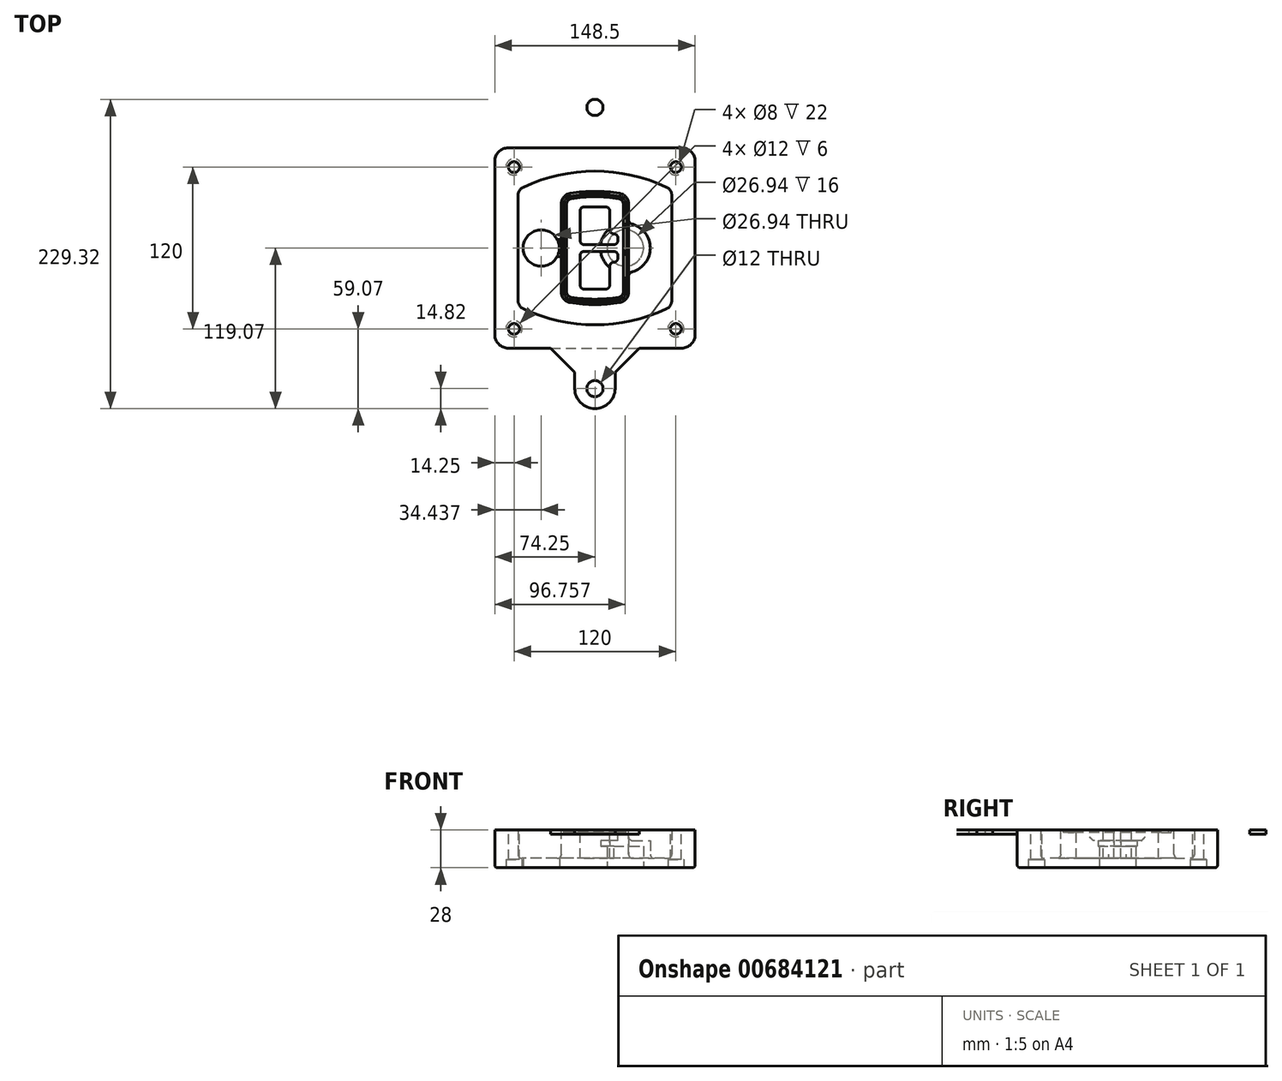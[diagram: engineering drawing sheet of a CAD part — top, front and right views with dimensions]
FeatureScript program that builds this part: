
annotation { "Feature Type Name" : "Feature", "Feature Type Description" : "" }
export const myFeature = defineFeature(function(context is Context, id is Id, definition is map)
    precondition{}
    {
        {
            var Q0;
            Q0=qCreatedBy(makeId("Top.planeOp"),FACE);
            var sketch = newSketch(context, id + "F0", { "sketchPlane" : qUnion([Q0])});
            skPoint(sketch, "E0.rect.middle", {"position": v(0, 0) * mm});
            skLineSegment(sketch, "E1.bottom", {"start": v(-64.25, -74.25) * mm, "end": v(64.25, -74.25) * mm});
            skLineSegment(sketch, "E1.top", {"start": v(-64.25, 74.25) * mm, "end": v(64.25, 74.25) * mm});
            skLineSegment(sketch, "E1.left", {"start": v(-74.25, -64.25) * mm, "end": v(-74.25, 64.25) * mm});
            skLineSegment(sketch, "E1.right", {"start": v(74.25, -64.25) * mm, "end": v(74.25, 64.25) * mm});
            skLineSegment(sketch, "E2", {"start": v(-74.25, 74.25) * mm, "end": v(74.25, -74.25) * mm, "construction": true});
            skLineSegment(sketch, "E3", {"start": v(74.25, 74.25) * mm, "end": v(-74.25, -74.25) * mm, "construction": true});
            skCircle(sketch, "E4", {"center": v(-60, 60) * mm, "radius": 4 * mm});
            skCircle(sketch, "E5", {"center": v(60, 60) * mm, "radius": 4 * mm});
            skCircle(sketch, "E6", {"center": v(60, -60) * mm, "radius": 4 * mm});
            skCircle(sketch, "E7", {"center": v(-60, -60) * mm, "radius": 4 * mm});
            skLineSegment(sketch, "E8", {"start": v(-60, 60) * mm, "end": v(60, 60) * mm, "construction": true});
            skLineSegment(sketch, "E9", {"start": v(60, 60) * mm, "end": v(60, -60) * mm, "construction": true});
            skLineSegment(sketch, "E10", {"start": v(60, -60) * mm, "end": v(-60, -60) * mm, "construction": true});
            skLineSegment(sketch, "E11", {"start": v(-60, -60) * mm, "end": v(-60, 60) * mm, "construction": true});
            skLineSegment(sketch, "E12", {"start": v(-60, 38.83) * mm, "end": v(-60, -38.83) * mm});
            skLineSegment(sketch, "E13", {"start": v(60, 38.83) * mm, "end": v(60, -38.83) * mm});
            skArc(sketch, "E14", {"start": v(54.26, 47.88) * mm, "mid": v(0, 60) * mm, "end": v(-54.26, 47.88) * mm});
            skArc(sketch, "E15", {"start": v(-54.26, -47.88) * mm, "mid": v(0, -60) * mm, "end": v(54.26, -47.88) * mm});
            skLineSegment(sketch, "E16", {"start": v(-60, 0) * mm, "end": v(60, 0) * mm, "construction": true});
            skPoint(sketch, "E17.visualSharp", {"position": v(-60, -45) * mm});
            skArc(sketch, "E17.filletArc", {"start": v(-60, -38.83) * mm, "mid": v(-58.44, -44.2) * mm, "end": v(-54.26, -47.88) * mm});
            skPoint(sketch, "E18.visualSharp", {"position": v(-60, 45) * mm});
            skArc(sketch, "E18.filletArc", {"start": v(-54.26, 47.88) * mm, "mid": v(-58.44, 44.2) * mm, "end": v(-60, 38.83) * mm});
            skPoint(sketch, "E19.visualSharp", {"position": v(60, 45) * mm});
            skArc(sketch, "E19.filletArc", {"start": v(60, 38.83) * mm, "mid": v(58.44, 44.2) * mm, "end": v(54.26, 47.88) * mm});
            skPoint(sketch, "E20.visualSharp", {"position": v(60, -45) * mm});
            skArc(sketch, "E20.filletArc", {"start": v(54.26, -47.88) * mm, "mid": v(58.44, -44.2) * mm, "end": v(60, -38.83) * mm});
            skPoint(sketch, "E21.visualSharp", {"position": v(-74.25, 74.25) * mm});
            skArc(sketch, "E21.filletArc", {"start": v(-64.25, 74.25) * mm, "mid": v(-71.32, 71.32) * mm, "end": v(-74.25, 64.25) * mm});
            skPoint(sketch, "E22.visualSharp", {"position": v(74.25, 74.25) * mm});
            skArc(sketch, "E22.filletArc", {"start": v(74.25, 64.25) * mm, "mid": v(71.32, 71.32) * mm, "end": v(64.25, 74.25) * mm});
            skPoint(sketch, "E23.visualSharp", {"position": v(74.25, -74.25) * mm});
            skArc(sketch, "E23.filletArc", {"start": v(64.25, -74.25) * mm, "mid": v(71.32, -71.32) * mm, "end": v(74.25, -64.25) * mm});
            skPoint(sketch, "E24.visualSharp", {"position": v(-74.25, -74.25) * mm});
            skArc(sketch, "E24.filletArc", {"start": v(-74.25, -64.25) * mm, "mid": v(-71.32, -71.32) * mm, "end": v(-64.25, -74.25) * mm});
            skArc(sketch, "E25.0", {"start": v(57, 38.83) * mm, "mid": v(55.9, 42.58) * mm, "end": v(52.98, 45.17) * mm});
            skLineSegment(sketch, "E25.1", {"start": v(57, 38.83) * mm, "end": v(57, -38.83) * mm});
            skArc(sketch, "E25.2", {"start": v(52.98, -45.17) * mm, "mid": v(55.9, -42.58) * mm, "end": v(57, -38.83) * mm});
            skArc(sketch, "E25.3", {"start": v(-52.98, -45.17) * mm, "mid": v(0, -57) * mm, "end": v(52.98, -45.17) * mm});
            skArc(sketch, "E25.4", {"start": v(-57, -38.83) * mm, "mid": v(-55.9, -42.58) * mm, "end": v(-52.98, -45.17) * mm});
            skArc(sketch, "E25.5", {"start": v(52.98, 45.17) * mm, "mid": v(0, 57) * mm, "end": v(-52.98, 45.17) * mm});
            skLineSegment(sketch, "E25.6", {"start": v(-57, 38.83) * mm, "end": v(-57, -38.83) * mm});
            skArc(sketch, "E25.7", {"start": v(-52.98, 45.17) * mm, "mid": v(-55.9, 42.58) * mm, "end": v(-57, 38.83) * mm});
            skArc(sketch, "E26.0", {"start": v(-55.96, 51.5) * mm, "mid": v(-61.82, 46.33) * mm, "end": v(-64, 38.83) * mm});
            skArc(sketch, "E26.1", {"start": v(55.96, 51.5) * mm, "mid": v(0, 64) * mm, "end": v(-55.96, 51.5) * mm});
            skArc(sketch, "E26.2", {"start": v(64, 38.83) * mm, "mid": v(61.82, 46.33) * mm, "end": v(55.96, 51.5) * mm});
            skLineSegment(sketch, "E26.3", {"start": v(64, 38.83) * mm, "end": v(64, -38.83) * mm});
            skArc(sketch, "E26.4", {"start": v(55.96, -51.5) * mm, "mid": v(61.82, -46.33) * mm, "end": v(64, -38.83) * mm});
            skLineSegment(sketch, "E26.5", {"start": v(-64, 38.83) * mm, "end": v(-64, -38.83) * mm});
            skArc(sketch, "E26.6", {"start": v(-55.96, -51.5) * mm, "mid": v(0, -64) * mm, "end": v(55.96, -51.5) * mm});
            skArc(sketch, "E26.7", {"start": v(-64, -38.83) * mm, "mid": v(-61.82, -46.33) * mm, "end": v(-55.96, -51.5) * mm});
            skSolve(sketch);
        }
        {
            var Q0;
            Q0=makeQuery(id+"F0.imprint","IMPRINT",FACE,{"disambiguationData":[TD([[makeQuery(id+"F0.imprint","IMPRINT",EDGE,{"derivedFrom":sQuery(id+"F0.wireOp",EDGE,"E1.bottom")}),1.0]])]});
            var Q1;
            Q1=makeQuery(id+"F0.imprint","IMPRINT",FACE,{"disambiguationData":[TD([[makeQuery(id+"F0.imprint","IMPRINT",EDGE,{"derivedFrom":sQuery(id+"F0.wireOp",EDGE,"E12")}),1.0]])]});
            var Q2;
            Q2=makeQuery(id+"F0.imprint","IMPRINT",FACE,{"disambiguationData":[TD([[makeQuery(id+"F0.imprint","IMPRINT",EDGE,{"derivedFrom":sQuery(id+"F0.wireOp",EDGE,"E25.0")}),1.0]])]});
            var Q3;
            Q3=makeQuery(id+"F0.imprint","IMPRINT",FACE,{"disambiguationData":[TD([[makeQuery(id+"F0.imprint","IMPRINT",EDGE,{"derivedFrom":sQuery(id+"F0.wireOp",EDGE,"E12")}),-1.0]])]});
            extrude(context, id + "F1", {"entities" : qUnion([Q0, Q1, Q2, Q3]), "oppositeDirection" : true, "depth" : 25 * mm, "offsetDistance" : 25 * mm});
        }
        {
            var Q0;
            Q0=makeQuery(id+"F0.imprint","IMPRINT",FACE,{"disambiguationData":[TD([[makeQuery(id+"F0.imprint","IMPRINT",EDGE,{"derivedFrom":sQuery(id+"F0.wireOp",EDGE,"E12")}),1.0]])]});
            extrude(context, id + "F2", {"entities" : qUnion([Q0]), "operationType" : NewBodyOperationType.ADD, "depth" : 3 * mm});
        }
        {
            var Q0;
            Q0=makeQuery(id+"F0.imprint","IMPRINT",FACE,{"disambiguationData":[TD([[makeQuery(id+"F0.imprint","IMPRINT",EDGE,{"derivedFrom":sQuery(id+"F0.wireOp",EDGE,"E25.0")}),1.0]])]});
            extrude(context, id + "F3", {"entities" : qUnion([Q0]), "operationType" : NewBodyOperationType.REMOVE, "oppositeDirection" : true, "depth" : 18 * mm});
        }
        {
            var Q0;
            Q0=makeQuery(id+"F2.opExtrude","CAP_FACE",FACE,{"disambiguationData":[OSD([sQuery(id+"F0.wireOp",EDGE,"E12"),sQuery(id+"F0.wireOp",EDGE,"E13"),sQuery(id+"F0.wireOp",EDGE,"E14"),sQuery(id+"F0.wireOp",EDGE,"E15"),sQuery(id+"F0.wireOp",EDGE,"E17.filletArc"),sQuery(id+"F0.wireOp",EDGE,"E18.filletArc"),sQuery(id+"F0.wireOp",EDGE,"E19.filletArc"),sQuery(id+"F0.wireOp",EDGE,"E20.filletArc"),sQuery(id+"F0.wireOp",EDGE,"E25.0"),sQuery(id+"F0.wireOp",EDGE,"E25.1"),sQuery(id+"F0.wireOp",EDGE,"E25.2"),sQuery(id+"F0.wireOp",EDGE,"E25.3"),sQuery(id+"F0.wireOp",EDGE,"E25.4"),sQuery(id+"F0.wireOp",EDGE,"E25.5"),sQuery(id+"F0.wireOp",EDGE,"E25.6"),sQuery(id+"F0.wireOp",EDGE,"E25.7")])],"isStart":false});
            var sketch = newSketch(context, id + "F4", { "sketchPlane" : qUnion([Q0])});
            skArc(sketch, "E27.0", {"start": v(-18.34, -40.45) * mm, "mid": v(0, -42) * mm, "end": v(18.34, -40.45) * mm});
            skArc(sketch, "E28.0", {"start": v(18.34, 40.45) * mm, "mid": v(0, 42) * mm, "end": v(-18.34, 40.45) * mm});
            skLineSegment(sketch, "E29", {"start": v(-25, 32.57) * mm, "end": v(-25, -32.57) * mm});
            skLineSegment(sketch, "E30", {"start": v(25, 32.57) * mm, "end": v(25, -32.57) * mm});
            skLineSegment(sketch, "E31", {"start": v(-25, 39.1) * mm, "end": v(25, 39.1) * mm, "construction": true});
            skLineSegment(sketch, "E32", {"start": v(-25, -39.1) * mm, "end": v(25, -39.1) * mm, "construction": true});
            skPoint(sketch, "E33.visualSharp", {"position": v(-25, 39.1) * mm});
            skArc(sketch, "E33.filletArc", {"start": v(-18.34, 40.45) * mm, "mid": v(-23.11, 37.73) * mm, "end": v(-25, 32.57) * mm});
            skPoint(sketch, "E34.visualSharp", {"position": v(25, 39.1) * mm});
            skArc(sketch, "E34.filletArc", {"start": v(25, 32.57) * mm, "mid": v(23.11, 37.73) * mm, "end": v(18.34, 40.45) * mm});
            skPoint(sketch, "E35.visualSharp", {"position": v(25, -39.1) * mm});
            skArc(sketch, "E35.filletArc", {"start": v(18.34, -40.45) * mm, "mid": v(23.11, -37.73) * mm, "end": v(25, -32.57) * mm});
            skPoint(sketch, "E36.visualSharp", {"position": v(-25, -39.1) * mm});
            skArc(sketch, "E36.filletArc", {"start": v(-25, -32.57) * mm, "mid": v(-23.11, -37.73) * mm, "end": v(-18.34, -40.45) * mm});
            skArc(sketch, "E37.0", {"start": v(52.98, 45.17) * mm, "mid": v(0, 57) * mm, "end": v(-52.98, 45.17) * mm});
            skArc(sketch, "E37.1", {"start": v(-52.98, 45.17) * mm, "mid": v(-55.9, 42.58) * mm, "end": v(-57, 38.83) * mm});
            skLineSegment(sketch, "E37.2", {"start": v(-57, 38.83) * mm, "end": v(-57, -38.83) * mm});
            skArc(sketch, "E37.3", {"start": v(-57, -38.83) * mm, "mid": v(-55.9, -42.58) * mm, "end": v(-52.98, -45.17) * mm});
            skArc(sketch, "E37.4", {"start": v(-52.98, -45.17) * mm, "mid": v(0, -57) * mm, "end": v(52.98, -45.17) * mm});
            skArc(sketch, "E37.5", {"start": v(52.98, -45.17) * mm, "mid": v(55.9, -42.58) * mm, "end": v(57, -38.83) * mm});
            skLineSegment(sketch, "E37.6", {"start": v(57, 38.83) * mm, "end": v(57, -38.83) * mm});
            skArc(sketch, "E37.7", {"start": v(57, 38.83) * mm, "mid": v(55.9, 42.58) * mm, "end": v(52.98, 45.17) * mm});
            skLineSegment(sketch, "E38.0", {"start": v(23, 32.57) * mm, "end": v(23, -32.57) * mm});
            skArc(sketch, "E38.1", {"start": v(18, -38.48) * mm, "mid": v(21.58, -36.44) * mm, "end": v(23, -32.57) * mm});
            skArc(sketch, "E38.2", {"start": v(-18, -38.48) * mm, "mid": v(0, -40) * mm, "end": v(18, -38.48) * mm});
            skArc(sketch, "E38.3", {"start": v(-23, -32.57) * mm, "mid": v(-21.58, -36.44) * mm, "end": v(-18, -38.48) * mm});
            skLineSegment(sketch, "E38.4", {"start": v(-23, 32.57) * mm, "end": v(-23, -32.57) * mm});
            skArc(sketch, "E38.5", {"start": v(23, 32.57) * mm, "mid": v(21.58, 36.44) * mm, "end": v(18, 38.48) * mm});
            skArc(sketch, "E38.6", {"start": v(-18, 38.48) * mm, "mid": v(-21.58, 36.44) * mm, "end": v(-23, 32.57) * mm});
            skArc(sketch, "E38.7", {"start": v(18, 38.48) * mm, "mid": v(0, 40) * mm, "end": v(-18, 38.48) * mm});
            skArc(sketch, "E39.0", {"start": v(21, 32.57) * mm, "mid": v(20.06, 35.15) * mm, "end": v(17.67, 36.5) * mm});
            skLineSegment(sketch, "E39.1", {"start": v(21, 32.57) * mm, "end": v(21, -32.57) * mm});
            skArc(sketch, "E39.2", {"start": v(17.67, -36.5) * mm, "mid": v(20.06, -35.15) * mm, "end": v(21, -32.57) * mm});
            skArc(sketch, "E39.3", {"start": v(-17.67, -36.5) * mm, "mid": v(0, -38) * mm, "end": v(17.67, -36.5) * mm});
            skArc(sketch, "E39.4", {"start": v(-21, -32.57) * mm, "mid": v(-20.06, -35.15) * mm, "end": v(-17.67, -36.5) * mm});
            skArc(sketch, "E39.5", {"start": v(17.67, 36.5) * mm, "mid": v(0, 38) * mm, "end": v(-17.67, 36.5) * mm});
            skLineSegment(sketch, "E39.6", {"start": v(-21, 32.57) * mm, "end": v(-21, -32.57) * mm});
            skArc(sketch, "E39.7", {"start": v(-17.67, 36.5) * mm, "mid": v(-20.06, 35.15) * mm, "end": v(-21, 32.57) * mm});
            skLineSegment(sketch, "E40", {"start": v(-25, 0) * mm, "end": v(25, 0) * mm, "construction": true});
            skLineSegment(sketch, "E41", {"start": v(-11, 5.5) * mm, "end": v(-11, 27.5) * mm});
            skLineSegment(sketch, "E42", {"start": v(-8, 30.5) * mm, "end": v(8, 30.5) * mm});
            skLineSegment(sketch, "E43", {"start": v(11, 27.5) * mm, "end": v(11, 13.5) * mm});
            skLineSegment(sketch, "E44", {"start": v(14, 10.5) * mm, "end": v(14, 10.5) * mm});
            skLineSegment(sketch, "E45", {"start": v(17, 7.5) * mm, "end": v(17, 5.5) * mm});
            skLineSegment(sketch, "E46", {"start": v(14, 2.5) * mm, "end": v(-8, 2.5) * mm});
            skPoint(sketch, "E47.visualSharp", {"position": v(-11, 30.5) * mm});
            skArc(sketch, "E47.filletArc", {"start": v(-8, 30.5) * mm, "mid": v(-10.12, 29.62) * mm, "end": v(-11, 27.5) * mm});
            skPoint(sketch, "E48.visualSharp", {"position": v(11, 30.5) * mm});
            skArc(sketch, "E48.filletArc", {"start": v(11, 27.5) * mm, "mid": v(10.12, 29.62) * mm, "end": v(8, 30.5) * mm});
            skPoint(sketch, "E49.visualSharp", {"position": v(11, 10.5) * mm});
            skArc(sketch, "E49.filletArc", {"start": v(11, 13.5) * mm, "mid": v(11.88, 11.38) * mm, "end": v(14, 10.5) * mm});
            skPoint(sketch, "E50.visualSharp", {"position": v(17, 10.5) * mm});
            skArc(sketch, "E50.filletArc", {"start": v(17, 7.5) * mm, "mid": v(16.12, 9.62) * mm, "end": v(14, 10.5) * mm});
            skPoint(sketch, "E51.visualSharp", {"position": v(17, 2.5) * mm});
            skArc(sketch, "E51.filletArc", {"start": v(14, 2.5) * mm, "mid": v(16.12, 3.38) * mm, "end": v(17, 5.5) * mm});
            skPoint(sketch, "E52.visualSharp", {"position": v(-11, 2.5) * mm});
            skArc(sketch, "E52.filletArc", {"start": v(-11, 5.5) * mm, "mid": v(-10.12, 3.38) * mm, "end": v(-8, 2.5) * mm});
            skLineSegment(sketch, "E53.0.MirrorCS", {"start": v(14, -2.5) * mm, "end": v(-8, -2.5) * mm});
            skArc(sketch, "E54.0.MirrorCS", {"start": v(-11, -5.5) * mm, "mid": v(-10.12, -3.38) * mm, "end": v(-8, -2.5) * mm});
            skLineSegment(sketch, "E55.0.MirrorCS", {"start": v(-11, -5.5) * mm, "end": v(-11, -27.5) * mm});
            skArc(sketch, "E56.0.MirrorCS", {"start": v(-8, -30.5) * mm, "mid": v(-10.12, -29.62) * mm, "end": v(-11, -27.5) * mm});
            skLineSegment(sketch, "E57.0.MirrorCS", {"start": v(-8, -30.5) * mm, "end": v(8, -30.5) * mm});
            skArc(sketch, "E58.0.MirrorCS", {"start": v(11, -27.5) * mm, "mid": v(10.12, -29.62) * mm, "end": v(8, -30.5) * mm});
            skLineSegment(sketch, "E59.0.MirrorCS", {"start": v(11, -27.5) * mm, "end": v(11, -13.5) * mm});
            skArc(sketch, "E60.0.MirrorCS", {"start": v(11, -13.5) * mm, "mid": v(11.88, -11.38) * mm, "end": v(14, -10.5) * mm});
            skArc(sketch, "E61.0.MirrorCS", {"start": v(17, -7.5) * mm, "mid": v(16.12, -9.62) * mm, "end": v(14, -10.5) * mm});
            skLineSegment(sketch, "E62.0.MirrorCS", {"start": v(17, -7.5) * mm, "end": v(17, -5.5) * mm});
            skArc(sketch, "E63.0.MirrorCS", {"start": v(14, -2.5) * mm, "mid": v(16.12, -3.38) * mm, "end": v(17, -5.5) * mm});
            skSolve(sketch);
        }
        {
            var Q0;
            Q0=makeQuery(id+"F4.imprint","IMPRINT",FACE,{"disambiguationData":[TD([[makeQuery(id+"F4.imprint","IMPRINT",EDGE,{"derivedFrom":sQuery(id+"F4.wireOp",EDGE,"E27.0")}),1.0]])]});
            var Q1;
            Q1=makeQuery(id+"F4.imprint","IMPRINT",FACE,{"disambiguationData":[TD([[makeQuery(id+"F4.imprint","IMPRINT",EDGE,{"derivedFrom":sQuery(id+"F4.wireOp",EDGE,"E38.0")}),-1.0]])]});
            var Q2;
            Q2=makeQuery(id+"F4.imprint","IMPRINT",FACE,{"disambiguationData":[TD([[makeQuery(id+"F4.imprint","IMPRINT",EDGE,{"derivedFrom":sQuery(id+"F4.wireOp",EDGE,"E39.0")}),1.0]])]});
            extrude(context, id + "F5", {"entities" : qUnion([Q0, Q1, Q2]), "operationType" : NewBodyOperationType.ADD, "endBound" : BoundingType.UP_TO_NEXT, "oppositeDirection" : true, "depth" : 25 * mm});
        }
        {
            var Q0;
            Q0=makeQuery(id+"F4.imprint","IMPRINT",FACE,{"disambiguationData":[TD([[makeQuery(id+"F4.imprint","IMPRINT",EDGE,{"derivedFrom":sQuery(id+"F4.wireOp",EDGE,"E38.0")}),-1.0]])]});
            extrude(context, id + "F6", {"entities" : qUnion([Q0]), "operationType" : NewBodyOperationType.REMOVE, "oppositeDirection" : true, "depth" : 2 * mm});
        }
        {
            var Q0;
            Q0=makeQuery(id+"F1.opExtrude","CAP_FACE",FACE,{"disambiguationData":[OSD([sQuery(id+"F0.wireOp",EDGE,"E1.bottom"),sQuery(id+"F0.wireOp",EDGE,"E1.top"),sQuery(id+"F0.wireOp",EDGE,"E1.left"),sQuery(id+"F0.wireOp",EDGE,"E1.right"),sQuery(id+"F0.wireOp",EDGE,"E4"),sQuery(id+"F0.wireOp",EDGE,"E5"),sQuery(id+"F0.wireOp",EDGE,"E6"),sQuery(id+"F0.wireOp",EDGE,"E7"),sQuery(id+"F0.wireOp",EDGE,"E21.filletArc"),sQuery(id+"F0.wireOp",EDGE,"E22.filletArc"),sQuery(id+"F0.wireOp",EDGE,"E23.filletArc"),sQuery(id+"F0.wireOp",EDGE,"E24.filletArc")])],"isStart":false});
            var sketch = newSketch(context, id + "F7", { "sketchPlane" : qUnion([Q0])});
            skCircle(sketch, "E64", {"center": v(22.5, 0) * mm, "radius": 13.47 * mm});
            skCircle(sketch, "E65", {"center": v(-39.81, 0) * mm, "radius": 13.47 * mm});
            skLineSegment(sketch, "E66", {"start": v(74.25, 0) * mm, "end": v(-74.25, 0) * mm});
            skCircle(sketch, "E67", {"center": v(22.5, 0) * mm, "radius": 18.47 * mm});
            skCircle(sketch, "E68", {"center": v(60, -60) * mm, "radius": 6 * mm});
            skCircle(sketch, "E69", {"center": v(-60, -60) * mm, "radius": 6 * mm});
            skCircle(sketch, "E70", {"center": v(-60, 60) * mm, "radius": 6 * mm});
            skCircle(sketch, "E71", {"center": v(60, 60) * mm, "radius": 6 * mm});
            skSolve(sketch);
        }
        {
            var Q0;
            {var subQ1=sQuery(id+"F7.wireOp",EDGE,"E66");var subQ4=sQuery(id+"F7.wireOp",EDGE,"E64");var subQ6=makeQuery(id+"F7.imprint","INTERSECT",VERTEX,{"disambiguationData":[OD(0.0)],"derivedFrom":[subQ4,subQ1]});Q0=makeQuery(id+"F7.imprint","IMPRINT",FACE,{"disambiguationData":[TD([[makeQuery(id+"F7.imprint","IMPRINT",EDGE,{"disambiguationData":[TD([[subQ6,-1.0]])],"derivedFrom":subQ4}),-1.0]])]});}
            var Q1;
            {var subQ0=sQuery(id+"F7.wireOp",EDGE,"E66");var subQ1=sQuery(id+"F7.wireOp",EDGE,"E64");var subQ3=makeQuery(id+"F7.imprint","INTERSECT",VERTEX,{"disambiguationData":[OD(0.0)],"derivedFrom":[subQ1,subQ0]});Q1=makeQuery(id+"F7.imprint","IMPRINT",FACE,{"disambiguationData":[TD([[makeQuery(id+"F7.imprint","IMPRINT",EDGE,{"disambiguationData":[TD([[subQ3,-1.0]])],"derivedFrom":subQ1}),1.0]])]});}
            var Q2;
            {var subQ0=sQuery(id+"F7.wireOp",EDGE,"E66");var subQ1=sQuery(id+"F7.wireOp",EDGE,"E64");var subQ3=makeQuery(id+"F7.imprint","INTERSECT",VERTEX,{"disambiguationData":[OD(0.0)],"derivedFrom":[subQ1,subQ0]});Q2=makeQuery(id+"F7.imprint","IMPRINT",FACE,{"disambiguationData":[TD([[makeQuery(id+"F7.imprint","IMPRINT",EDGE,{"disambiguationData":[TD([[subQ3,1.0]])],"derivedFrom":subQ1}),1.0]])]});}
            var Q3;
            {var subQ1=sQuery(id+"F7.wireOp",EDGE,"E66");var subQ4=sQuery(id+"F7.wireOp",EDGE,"E64");var subQ6=makeQuery(id+"F7.imprint","INTERSECT",VERTEX,{"disambiguationData":[OD(0.0)],"derivedFrom":[subQ4,subQ1]});Q3=makeQuery(id+"F7.imprint","IMPRINT",FACE,{"disambiguationData":[TD([[makeQuery(id+"F7.imprint","IMPRINT",EDGE,{"disambiguationData":[TD([[subQ6,1.0]])],"derivedFrom":subQ4}),-1.0]])]});}
            extrude(context, id + "F8", {"entities" : qUnion([Q0, Q1, Q2, Q3]), "operationType" : NewBodyOperationType.ADD, "oppositeDirection" : true, "depth" : 20 * mm});
        }
        {
            var Q0;
            {var subQ0=sQuery(id+"F7.wireOp",EDGE,"E66");var subQ1=sQuery(id+"F7.wireOp",EDGE,"E64");var subQ3=makeQuery(id+"F7.imprint","INTERSECT",VERTEX,{"disambiguationData":[OD(0.0)],"derivedFrom":[subQ1,subQ0]});Q0=makeQuery(id+"F7.imprint","IMPRINT",FACE,{"disambiguationData":[TD([[makeQuery(id+"F7.imprint","IMPRINT",EDGE,{"disambiguationData":[TD([[subQ3,-1.0]])],"derivedFrom":subQ1}),1.0]])]});}
            var Q1;
            {var subQ0=sQuery(id+"F7.wireOp",EDGE,"E66");var subQ1=sQuery(id+"F7.wireOp",EDGE,"E64");var subQ3=makeQuery(id+"F7.imprint","INTERSECT",VERTEX,{"disambiguationData":[OD(0.0)],"derivedFrom":[subQ1,subQ0]});Q1=makeQuery(id+"F7.imprint","IMPRINT",FACE,{"disambiguationData":[TD([[makeQuery(id+"F7.imprint","IMPRINT",EDGE,{"disambiguationData":[TD([[subQ3,1.0]])],"derivedFrom":subQ1}),1.0]])]});}
            extrude(context, id + "F9", {"entities" : qUnion([Q0, Q1]), "operationType" : NewBodyOperationType.REMOVE, "oppositeDirection" : true, "depth" : 16 * mm});
        }
        {
            var Q0;
            {var subQ0=sQuery(id+"F7.wireOp",EDGE,"E66");var subQ1=sQuery(id+"F7.wireOp",EDGE,"E65");var subQ3=makeQuery(id+"F7.imprint","INTERSECT",VERTEX,{"disambiguationData":[OD(0.0)],"derivedFrom":[subQ1,subQ0]});Q0=makeQuery(id+"F7.imprint","IMPRINT",FACE,{"disambiguationData":[TD([[makeQuery(id+"F7.imprint","IMPRINT",EDGE,{"disambiguationData":[TD([[subQ3,-1.0]])],"derivedFrom":subQ1}),1.0]])]});}
            var Q1;
            {var subQ0=sQuery(id+"F7.wireOp",EDGE,"E66");var subQ1=sQuery(id+"F7.wireOp",EDGE,"E65");var subQ3=makeQuery(id+"F7.imprint","INTERSECT",VERTEX,{"disambiguationData":[OD(0.0)],"derivedFrom":[subQ1,subQ0]});Q1=makeQuery(id+"F7.imprint","IMPRINT",FACE,{"disambiguationData":[TD([[makeQuery(id+"F7.imprint","IMPRINT",EDGE,{"disambiguationData":[TD([[subQ3,1.0]])],"derivedFrom":subQ1}),1.0]])]});}
            extrude(context, id + "F10", {"entities" : qUnion([Q0, Q1]), "operationType" : NewBodyOperationType.REMOVE, "oppositeDirection" : true, "depth" : 25 * mm});
        }
        {
            var Q0;
            Q0=makeQuery(id+"F7.imprint","IMPRINT",FACE,{"disambiguationData":[TD([[makeQuery(id+"F7.imprint","IMPRINT",EDGE,{"derivedFrom":sQuery(id+"F7.wireOp",EDGE,"E68")}),1.0]])]});
            var Q1;
            Q1=makeQuery(id+"F7.imprint","IMPRINT",FACE,{"disambiguationData":[TD([[makeQuery(id+"F7.imprint","IMPRINT",EDGE,{"derivedFrom":makeQuery(id+"F1.opExtrude","CAP_EDGE",EDGE,{"disambiguationData":[OSD([sQuery(id+"F0.wireOp",EDGE,"E5")])],"isStart":false})}),-1.0]])]});
            var Q2;
            Q2=makeQuery(id+"F7.imprint","IMPRINT",FACE,{"disambiguationData":[TD([[makeQuery(id+"F7.imprint","IMPRINT",EDGE,{"derivedFrom":sQuery(id+"F7.wireOp",EDGE,"E69")}),1.0]])]});
            var Q3;
            Q3=makeQuery(id+"F7.imprint","IMPRINT",FACE,{"disambiguationData":[TD([[makeQuery(id+"F7.imprint","IMPRINT",EDGE,{"derivedFrom":makeQuery(id+"F1.opExtrude","CAP_EDGE",EDGE,{"disambiguationData":[OSD([sQuery(id+"F0.wireOp",EDGE,"E4")])],"isStart":false})}),-1.0]])]});
            var Q4;
            Q4=makeQuery(id+"F7.imprint","IMPRINT",FACE,{"disambiguationData":[TD([[makeQuery(id+"F7.imprint","IMPRINT",EDGE,{"derivedFrom":sQuery(id+"F7.wireOp",EDGE,"E70")}),1.0]])]});
            var Q5;
            Q5=makeQuery(id+"F7.imprint","IMPRINT",FACE,{"disambiguationData":[TD([[makeQuery(id+"F7.imprint","IMPRINT",EDGE,{"derivedFrom":makeQuery(id+"F1.opExtrude","CAP_EDGE",EDGE,{"disambiguationData":[OSD([sQuery(id+"F0.wireOp",EDGE,"E7")])],"isStart":false})}),-1.0]])]});
            var Q6;
            Q6=makeQuery(id+"F7.imprint","IMPRINT",FACE,{"disambiguationData":[TD([[makeQuery(id+"F7.imprint","IMPRINT",EDGE,{"derivedFrom":sQuery(id+"F7.wireOp",EDGE,"E71")}),1.0]])]});
            var Q7;
            Q7=makeQuery(id+"F7.imprint","IMPRINT",FACE,{"disambiguationData":[TD([[makeQuery(id+"F7.imprint","IMPRINT",EDGE,{"derivedFrom":makeQuery(id+"F1.opExtrude","CAP_EDGE",EDGE,{"disambiguationData":[OSD([sQuery(id+"F0.wireOp",EDGE,"E6")])],"isStart":false})}),-1.0]])]});
            extrude(context, id + "F11", {"entities" : qUnion([Q0, Q1, Q2, Q3, Q4, Q5, Q6, Q7]), "operationType" : NewBodyOperationType.REMOVE, "oppositeDirection" : true, "depth" : 6 * mm});
        }
        {
            var Q0;
            Q0=makeQuery(id+"F9.boolean.opBoolean","COPY",FACE,{"derivedFrom":makeQuery(id+"F9.opExtrude","CAP_FACE",FACE,{"disambiguationData":[OSD([sQuery(id+"F7.wireOp",EDGE,"E64")])],"isStart":false})});
            var sketch = newSketch(context, id + "F12", { "sketchPlane" : qUnion([Q0])});
            skArc(sketch, "E72.0", {"start": v(11, 14.45) * mm, "mid": v(6.45, 9.13) * mm, "end": v(4.2, 2.5) * mm});
            skArc(sketch, "E72.1", {"start": v(4.2, -2.5) * mm, "mid": v(6.45, -9.13) * mm, "end": v(11, -14.45) * mm});
            skLineSegment(sketch, "E73", {"start": v(4.2, -2.5) * mm, "end": v(14, -2.5) * mm});
            skLineSegment(sketch, "E74.0", {"start": v(14, 2.5) * mm, "end": v(4.2, 2.5) * mm});
            skArc(sketch, "E74.1", {"start": v(14, 2.5) * mm, "mid": v(16.12, 3.38) * mm, "end": v(17, 5.5) * mm});
            skLineSegment(sketch, "E74.2", {"start": v(17, 7.5) * mm, "end": v(17, 5.5) * mm});
            skArc(sketch, "E74.3", {"start": v(17, 7.5) * mm, "mid": v(16.12, 9.62) * mm, "end": v(14, 10.5) * mm});
            skArc(sketch, "E74.4", {"start": v(11, 13.5) * mm, "mid": v(11.88, 11.38) * mm, "end": v(14, 10.5) * mm});
            skLineSegment(sketch, "E74.5", {"start": v(11, 14.45) * mm, "end": v(11, 13.5) * mm});
            skLineSegment(sketch, "E74.7", {"start": v(14, -2.5) * mm, "end": v(4.2, -2.5) * mm});
            skArc(sketch, "E74.8", {"start": v(14, -2.5) * mm, "mid": v(16.12, -3.38) * mm, "end": v(17, -5.5) * mm});
            skLineSegment(sketch, "E74.9", {"start": v(17, -7.5) * mm, "end": v(17, -5.5) * mm});
            skArc(sketch, "E74.10", {"start": v(17, -7.5) * mm, "mid": v(16.12, -9.62) * mm, "end": v(14, -10.5) * mm});
            skArc(sketch, "E74.11", {"start": v(11, -13.5) * mm, "mid": v(11.88, -11.38) * mm, "end": v(14, -10.5) * mm});
            skLineSegment(sketch, "E74.12", {"start": v(11, -14.45) * mm, "end": v(11, -13.5) * mm});
            skPoint(sketch, "E75.orphan", {"position": v(11, -27.5) * mm});
            skPoint(sketch, "E76.orphan", {"position": v(-8, -2.5) * mm});
            skPoint(sketch, "E77.orphan", {"position": v(-8, 2.5) * mm});
            skPoint(sketch, "E78.orphan", {"position": v(11, 27.5) * mm});
            skSolve(sketch);
        }
        {
            var Q0;
            {var subQ7=sQuery(id+"F12.wireOp",EDGE,"E72.0");var subQ14=sQuery(id+"F12.wireOp",EDGE,"E72.1");var subQ16=sQuery(id+"F12.wireOp",EDGE,"E74.1");var subQ18=sQuery(id+"F12.wireOp",EDGE,"E74.8");Q0=qUnion([makeQuery(id+"F12.imprint","IMPRINT",FACE,{"disambiguationData":[TD([[makeQuery(id+"F12.imprint","IMPRINT",EDGE,{"derivedFrom":subQ7}),1.0]])]}),makeQuery(id+"F12.imprint","IMPRINT",FACE,{"disambiguationData":[TD([[makeQuery(id+"F12.imprint","IMPRINT",EDGE,{"derivedFrom":subQ14}),1.0]])]}),makeQuery(id+"F12.imprint","IMPRINT",FACE,{"disambiguationData":[TD([[makeQuery(id+"F12.imprint","IMPRINT",EDGE,{"derivedFrom":subQ16}),1.0]])]}),makeQuery(id+"F12.imprint","IMPRINT",FACE,{"disambiguationData":[TD([[makeQuery(id+"F12.imprint","IMPRINT",EDGE,{"derivedFrom":subQ18}),-1.0]])]})]);}
            var Q1;
            Q1=makeQuery(id+"F5.boolean.opBoolean","SPLIT",FACE,{"disambiguationData":[TD([makeQuery(id+"F5.opExtrude","SWEPT_FACE",FACE,{"disambiguationData":[OSD([sQuery(id+"F4.wireOp",EDGE,"E41")])]})])],"derivedFrom":makeQuery(id+"F3.boolean.opBoolean","COPY",FACE,{"derivedFrom":makeQuery(id+"F3.opExtrude","CAP_FACE",FACE,{"disambiguationData":[OSD([sQuery(id+"F0.wireOp",EDGE,"E25.0"),sQuery(id+"F0.wireOp",EDGE,"E25.1"),sQuery(id+"F0.wireOp",EDGE,"E25.2"),sQuery(id+"F0.wireOp",EDGE,"E25.3"),sQuery(id+"F0.wireOp",EDGE,"E25.4"),sQuery(id+"F0.wireOp",EDGE,"E25.5"),sQuery(id+"F0.wireOp",EDGE,"E25.6"),sQuery(id+"F0.wireOp",EDGE,"E25.7")])],"isStart":false})})});
            extrude(context, id + "F13", {"entities" : qUnion([Q0]), "operationType" : NewBodyOperationType.REMOVE, "endBound" : BoundingType.UP_TO_SURFACE, "endBoundEntityFace" : qUnion([Q1]), "depth" : 25 * mm});
        }
        {
            var Q0;
            Q0=makeQuery(id+"F3.boolean.opBoolean","COPY",EDGE,{"derivedFrom":makeQuery(id+"F3.opExtrude","CAP_EDGE",EDGE,{"disambiguationData":[OSD([sQuery(id+"F0.wireOp",EDGE,"E25.6")])],"isStart":false})});
            var Q1;
            Q1=makeQuery(id+"F8.boolean.opBoolean","INTERSECT",EDGE,{"derivedFrom":[makeQuery(id+"F5.opExtrude","SWEPT_FACE",FACE,{"disambiguationData":[OSD([sQuery(id+"F4.wireOp",EDGE,"E30")])]}),makeQuery(id+"F8.opExtrude","CAP_FACE",FACE,{"disambiguationData":[OSD([sQuery(id+"F7.wireOp",EDGE,"E67")])],"isStart":false})]});
            var Q2;
            Q2=makeQuery(id+"F8.boolean.opBoolean","INTERSECT",EDGE,{"disambiguationData":[OD(1.0)],"derivedFrom":[makeQuery(id+"F5.opExtrude","SWEPT_FACE",FACE,{"disambiguationData":[OSD([sQuery(id+"F4.wireOp",EDGE,"E30")])]}),makeQuery(id+"F8.opExtrude","SWEPT_FACE",FACE,{"disambiguationData":[OSD([sQuery(id+"F7.wireOp",EDGE,"E67")])]})]});
            var Q3;
            {var subQ0=sQuery(id+"F4.wireOp",EDGE,"E30");Q3=makeQuery(id+"F8.boolean.opBoolean","SPLIT",EDGE,{"disambiguationData":[TD([makeQuery(id+"F5.opExtrude","SWEPT_FACE",FACE,{"disambiguationData":[OSD([sQuery(id+"F4.wireOp",EDGE,"E35.filletArc")])]})])],"derivedFrom":makeQuery(id+"F5.opExtrude","CAP_EDGE",EDGE,{"disambiguationData":[OSD([subQ0])],"isStart":false})});}
            var Q4;
            {var subQ0=sQuery(id+"F0.wireOp",EDGE,"E25.7");var subQ1=sQuery(id+"F0.wireOp",EDGE,"E25.1");var subQ2=sQuery(id+"F0.wireOp",EDGE,"E25.6");var subQ3=sQuery(id+"F0.wireOp",EDGE,"E25.5");var subQ4=sQuery(id+"F0.wireOp",EDGE,"E25.4");var subQ5=sQuery(id+"F0.wireOp",EDGE,"E25.0");var subQ6=sQuery(id+"F0.wireOp",EDGE,"E25.2");var subQ7=sQuery(id+"F0.wireOp",EDGE,"E25.3");Q4=makeQuery(id+"F8.boolean.opBoolean","INTERSECT",EDGE,{"derivedFrom":[makeQuery(id+"F5.boolean.opBoolean","SPLIT",FACE,{"disambiguationData":[TD([makeQuery(id+"F2.opExtrude","SWEPT_FACE",FACE,{"disambiguationData":[OSD([subQ5])]})])],"derivedFrom":makeQuery(id+"F3.boolean.opBoolean","COPY",FACE,{"derivedFrom":makeQuery(id+"F3.opExtrude","CAP_FACE",FACE,{"disambiguationData":[OSD([subQ5,subQ1,subQ6,subQ7,subQ4,subQ3,subQ2,subQ0])],"isStart":false})})}),makeQuery(id+"F8.opExtrude","SWEPT_FACE",FACE,{"disambiguationData":[OSD([sQuery(id+"F7.wireOp",EDGE,"E67")])]})]});}
            var Q5;
            Q5=makeQuery(id+"F8.boolean.opBoolean","INTERSECT",EDGE,{"disambiguationData":[OD(0.0)],"derivedFrom":[makeQuery(id+"F5.opExtrude","SWEPT_FACE",FACE,{"disambiguationData":[OSD([sQuery(id+"F4.wireOp",EDGE,"E30")])]}),makeQuery(id+"F8.opExtrude","SWEPT_FACE",FACE,{"disambiguationData":[OSD([sQuery(id+"F7.wireOp",EDGE,"E67")])]})]});
            fillet(context, id + "F14", {"entities" : qUnion([Q0, Q1, Q2, Q3, Q4, Q5]), "radius" : 3 * mm, "tangentPropagation" : true, "allowEdgeOverflow" : false});
        }
        {
            var Q0;
            Q0=makeQuery(id+"F1.opExtrude","CAP_EDGE",EDGE,{"disambiguationData":[OSD([sQuery(id+"F0.wireOp",EDGE,"E1.bottom")])],"isStart":false});
            fillet(context, id + "F15", {"entities" : qUnion([Q0]), "radius" : 2 * mm, "tangentPropagation" : true, "allowEdgeOverflow" : false});
        }
        {
            var Q0;
            {var subQ0=sQuery(id+"F0.wireOp",EDGE,"E21.filletArc");var subQ1=sQuery(id+"F0.wireOp",EDGE,"E7");var subQ2=sQuery(id+"F0.wireOp",EDGE,"E6");var subQ3=sQuery(id+"F0.wireOp",EDGE,"E5");var subQ4=sQuery(id+"F0.wireOp",EDGE,"E4");var subQ5=sQuery(id+"F0.wireOp",EDGE,"E22.filletArc");var subQ6=sQuery(id+"F0.wireOp",EDGE,"E1.bottom");var subQ7=sQuery(id+"F0.wireOp",EDGE,"E1.right");var subQ8=sQuery(id+"F0.wireOp",EDGE,"E1.top");var subQ9=sQuery(id+"F0.wireOp",EDGE,"E1.left");var subQ10=sQuery(id+"F0.wireOp",EDGE,"E23.filletArc");var subQ11=sQuery(id+"F0.wireOp",EDGE,"E24.filletArc");Q0=makeQuery(id+"F2.boolean.opBoolean","SPLIT",FACE,{"disambiguationData":[TD([makeQuery(id+"F1.opExtrude","SWEPT_FACE",FACE,{"disambiguationData":[OSD([subQ6])]})])],"derivedFrom":makeQuery(id+"F1.opExtrude","CAP_FACE",FACE,{"disambiguationData":[OSD([subQ6,subQ8,subQ9,subQ7,subQ4,subQ3,subQ2,subQ1,subQ0,subQ5,subQ10,subQ11])],"isStart":true})});}
            var sketch = newSketch(context, id + "F16", { "sketchPlane" : qUnion([Q0])});
            skLineSegment(sketch, "E79", {"start": v(0, 74.25) * mm, "end": v(0, 104.25) * mm, "construction": true});
            skCircle(sketch, "E80", {"center": v(0, 104.25) * mm, "radius": 6 * mm});
            skArc(sketch, "E81", {"start": v(15, 104.25) * mm, "mid": v(0, 119.07) * mm, "end": v(-15, 104.25) * mm});
            skLineSegment(sketch, "E82", {"start": v(15, 104.25) * mm, "end": v(15.14, 92.25) * mm});
            skLineSegment(sketch, "E83", {"start": v(15.14, 92.25) * mm, "end": v(33.14, 74.25) * mm});
            skLineSegment(sketch, "E84", {"start": v(-15, 104.25) * mm, "end": v(-15, 92.25) * mm});
            skLineSegment(sketch, "E85", {"start": v(-33, 74.25) * mm, "end": v(-15, 92.25) * mm});
            skLineSegment(sketch, "E86", {"start": v(-74.25, 0) * mm, "end": v(74.25, 0) * mm, "construction": true});
            skLineSegment(sketch, "E87.MirrorCS", {"start": v(15, 104.25) * mm, "end": v(15, 92.25) * mm});
            skLineSegment(sketch, "E88.MirrorCS", {"start": v(-15, 104.25) * mm, "end": v(-15.14, 92.25) * mm});
            skArc(sketch, "E89.MirrorCS", {"start": v(-15, 104.25) * mm, "mid": v(0, 119.07) * mm, "end": v(15, 104.25) * mm});
            skLineSegment(sketch, "E90.MirrorCS", {"start": v(-15.14, 92.25) * mm, "end": v(-33.14, 74.25) * mm});
            skLineSegment(sketch, "E91.MirrorCS", {"start": v(33, 74.25) * mm, "end": v(15, 92.25) * mm});
            skLineSegment(sketch, "E92.MirrorCS", {"start": v(74.25, 0) * mm, "end": v(-74.25, 0) * mm, "construction": true});
            skLineSegment(sketch, "E93.MirrorCS", {"start": v(15, -104.25) * mm, "end": v(15.14, -92.25) * mm});
            skLineSegment(sketch, "E94.MirrorCS", {"start": v(-15, -104.25) * mm, "end": v(-15.14, -92.25) * mm});
            skLineSegment(sketch, "E95.MirrorCS", {"start": v(15, -104.25) * mm, "end": v(15, -92.25) * mm});
            skLineSegment(sketch, "E96.MirrorCS", {"start": v(-15, -104.25) * mm, "end": v(-15, -92.25) * mm});
            skCircle(sketch, "E97.MirrorC", {"center": v(0, -104.25) * mm, "radius": 6 * mm});
            skLineSegment(sketch, "E98.MirrorCS", {"start": v(-33, -74.25) * mm, "end": v(-15, -92.25) * mm});
            skLineSegment(sketch, "E99.MirrorCS", {"start": v(15.14, -92.25) * mm, "end": v(33.14, -74.25) * mm});
            skLineSegment(sketch, "E100.MirrorCS", {"start": v(-15.14, -92.25) * mm, "end": v(-33.14, -74.25) * mm});
            skLineSegment(sketch, "E101.MirrorCS", {"start": v(33, -74.25) * mm, "end": v(15, -92.25) * mm});
            skArc(sketch, "E102.MirrorCS", {"start": v(15, -104.25) * mm, "mid": v(0, -119.07) * mm, "end": v(-15, -104.25) * mm});
            skArc(sketch, "E103.MirrorCS", {"start": v(-15, -104.25) * mm, "mid": v(0, -119.07) * mm, "end": v(15, -104.25) * mm});
            skLineSegment(sketch, "E104.MirrorCS", {"start": v(0, -74.25) * mm, "end": v(0, -104.25) * mm, "construction": true});
            skSolve(sketch);
        }
        {
            var Q0;
            Q0=makeQuery(id+"F16.imprint","IMPRINT",FACE,{"disambiguationData":[TD([[makeQuery(id+"F16.imprint","IMPRINT",EDGE,{"derivedFrom":sQuery(id+"F16.wireOp",EDGE,"E80")}),1.0]])]});
            var Q1;
            {var subQ12=sQuery(id+"F16.wireOp",EDGE,"E98.MirrorCS");Q1=makeQuery(id+"F16.imprint","IMPRINT",FACE,{"disambiguationData":[TD([[makeQuery(id+"F16.imprint","IMPRINT",EDGE,{"derivedFrom":subQ12}),1.0]])]});}
            var Q2;
            Q2=makeQuery(id+"F16.imprint","IMPRINT",FACE,{"disambiguationData":[TD([[makeQuery(id+"F16.imprint","IMPRINT",EDGE,{"derivedFrom":makeQuery(id+"F1.opExtrude","CAP_EDGE",EDGE,{"disambiguationData":[OSD([sQuery(id+"F0.wireOp",EDGE,"E1.left")])],"isStart":true})}),-1.0]])]});
            var Q3;
            Q3=makeQuery(id+"F2.opExtrude","CAP_FACE",FACE,{"disambiguationData":[OSD([sQuery(id+"F0.wireOp",EDGE,"E12"),sQuery(id+"F0.wireOp",EDGE,"E13"),sQuery(id+"F0.wireOp",EDGE,"E14"),sQuery(id+"F0.wireOp",EDGE,"E15"),sQuery(id+"F0.wireOp",EDGE,"E17.filletArc"),sQuery(id+"F0.wireOp",EDGE,"E18.filletArc"),sQuery(id+"F0.wireOp",EDGE,"E19.filletArc"),sQuery(id+"F0.wireOp",EDGE,"E20.filletArc"),sQuery(id+"F0.wireOp",EDGE,"E25.0"),sQuery(id+"F0.wireOp",EDGE,"E25.1"),sQuery(id+"F0.wireOp",EDGE,"E25.2"),sQuery(id+"F0.wireOp",EDGE,"E25.3"),sQuery(id+"F0.wireOp",EDGE,"E25.4"),sQuery(id+"F0.wireOp",EDGE,"E25.5"),sQuery(id+"F0.wireOp",EDGE,"E25.6"),sQuery(id+"F0.wireOp",EDGE,"E25.7")])],"isStart":false});
            extrude(context, id + "F17", {"entities" : qUnion([Q0, Q1, Q2]), "operationType" : NewBodyOperationType.ADD, "endBound" : BoundingType.UP_TO_SURFACE, "depth" : 25 * mm, "endBoundEntityFace" : qUnion([Q3]), "offsetDistance" : 25 * mm});
        }
    });
